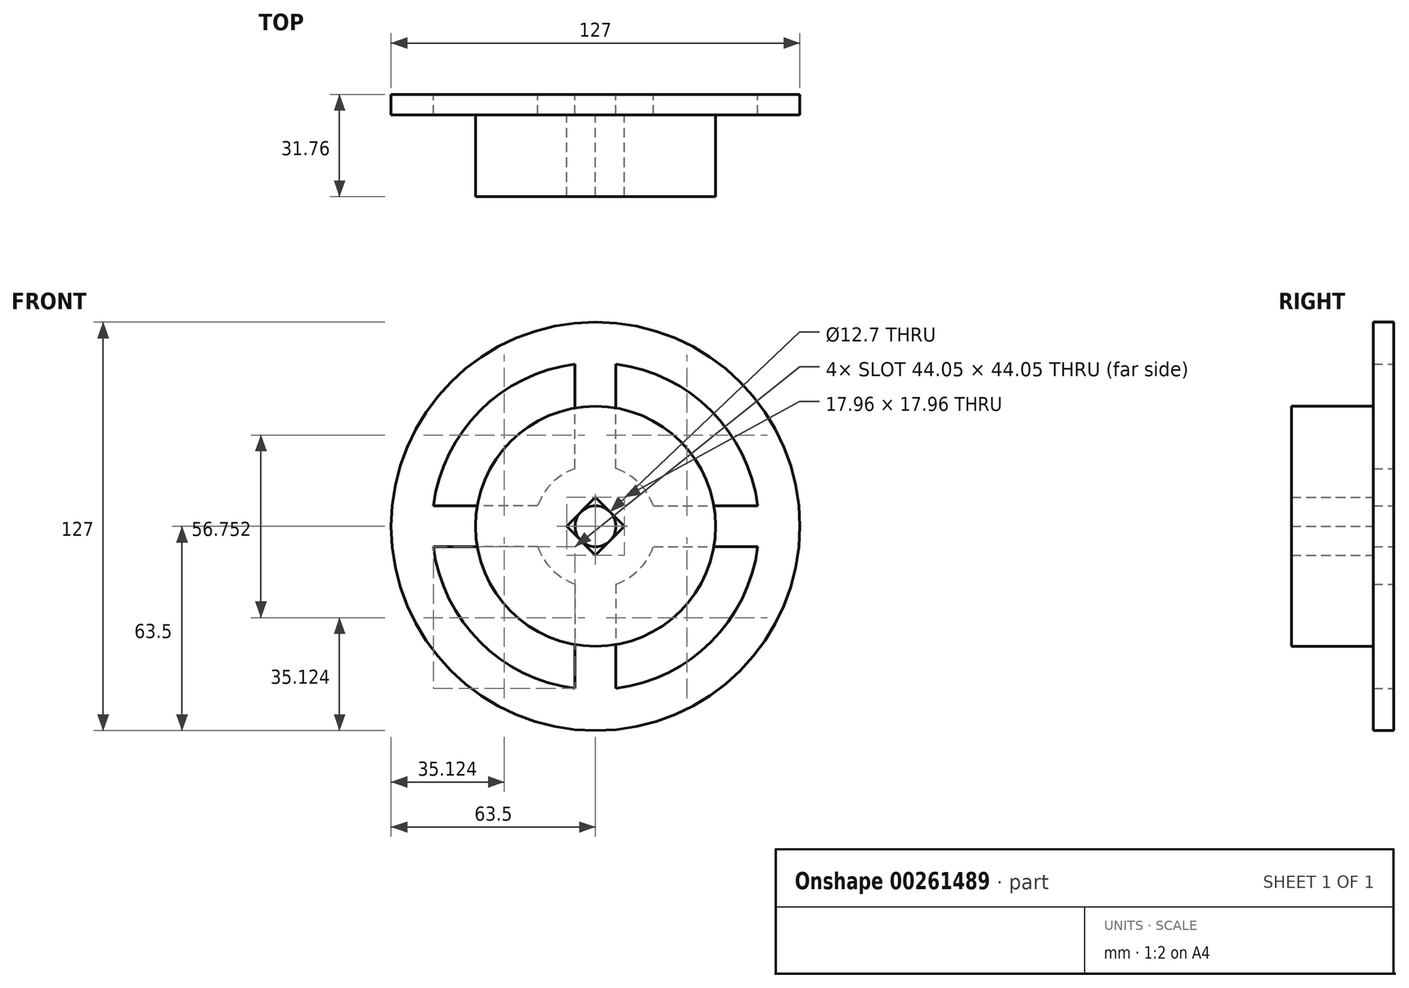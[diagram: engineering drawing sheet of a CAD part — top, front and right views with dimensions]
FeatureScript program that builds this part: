
annotation { "Feature Type Name" : "Feature", "Feature Type Description" : "" }
export const myFeature = defineFeature(function(context is Context, id is Id, definition is map)
    precondition{}
    {
        {
            var Q0;
            Q0=qCreatedBy(makeId("Front.planeOp"),FACE);
            var sketch = newSketch(context, id + "F0", { "sketchPlane" : qUnion([Q0])});
            skCircle(sketch, "E0", {"center": v(0, 0) * mm, "radius": 63.5 * mm});
            skArc(sketch, "E1", {"start": v(-50.4, -6.35) * mm, "mid": v(-35.92, -35.92) * mm, "end": v(-6.35, -50.4) * mm});
            skArc(sketch, "E2", {"start": v(17.96, 6.35) * mm, "mid": v(13.47, 13.47) * mm, "end": v(6.35, 17.96) * mm});
            skCircle(sketch, "E3", {"center": v(0, 0) * mm, "radius": 6.35 * mm});
            skLineSegment(sketch, "E4", {"start": v(0, 0) * mm, "end": v(0, 50.8) * mm, "construction": true});
            skLineSegment(sketch, "E5", {"start": v(0, 0) * mm, "end": v(50.8, 0) * mm, "construction": true});
            skLineSegment(sketch, "E6", {"start": v(0, 0) * mm, "end": v(0, -50.8) * mm, "construction": true});
            skLineSegment(sketch, "E7", {"start": v(0, 0) * mm, "end": v(-50.8, 0) * mm, "construction": true});
            skArc(sketch, "E8.trimOffspring", {"start": v(-6.35, 50.4) * mm, "mid": v(-35.92, 35.92) * mm, "end": v(-50.4, 6.35) * mm});
            skArc(sketch, "E9.trimOffspring", {"start": v(50.4, 6.35) * mm, "mid": v(35.92, 35.92) * mm, "end": v(6.35, 50.4) * mm});
            skArc(sketch, "E10.trimOffspring", {"start": v(6.35, -50.4) * mm, "mid": v(35.92, -35.92) * mm, "end": v(50.4, -6.35) * mm});
            skArc(sketch, "E11.trimOffspring", {"start": v(-6.35, 17.96) * mm, "mid": v(-13.47, 13.47) * mm, "end": v(-17.96, 6.35) * mm});
            skArc(sketch, "E12.trimOffspring", {"start": v(-17.96, -6.35) * mm, "mid": v(-13.47, -13.47) * mm, "end": v(-6.35, -17.96) * mm});
            skArc(sketch, "E13.trimOffspring", {"start": v(6.35, -17.96) * mm, "mid": v(13.47, -13.47) * mm, "end": v(17.96, -6.35) * mm});
            skLineSegment(sketch, "E14.trimOffspring", {"start": v(17.96, -6.35) * mm, "end": v(50.4, -6.35) * mm});
            skLineSegment(sketch, "E15.trimOffspring", {"start": v(6.35, -17.96) * mm, "end": v(6.35, -50.4) * mm});
            skLineSegment(sketch, "E16.trimOffspring", {"start": v(-6.35, -17.96) * mm, "end": v(-6.35, -50.4) * mm});
            skLineSegment(sketch, "E17.trimOffspring", {"start": v(-17.96, -6.35) * mm, "end": v(-50.4, -6.35) * mm});
            skLineSegment(sketch, "E18.trimOffspring", {"start": v(-17.96, 6.35) * mm, "end": v(-50.4, 6.35) * mm});
            skLineSegment(sketch, "E19.trimOffspring", {"start": v(-6.35, 17.96) * mm, "end": v(-6.35, 50.4) * mm});
            skLineSegment(sketch, "E20.trimOffspring", {"start": v(6.35, 17.96) * mm, "end": v(6.35, 50.4) * mm});
            skLineSegment(sketch, "E21.trimOffspring", {"start": v(17.96, 6.35) * mm, "end": v(50.4, 6.35) * mm});
            skLineSegment(sketch, "E22.0", {"start": v(-6.35, 17.96) * mm, "end": v(-6.35, 50.8) * mm});
            skSolve(sketch);
        }
        {
            var Q0;
            Q0=qSketchRegion(id+"F0",true);
            extrude(context, id + "F1", {"entities" : qUnion([Q0]), "endBound" : BoundingType.SYMMETRIC, "depth" : 6.35 * mm});
        }
        {
            var Q0;
            Q0=makeQuery(id+"F1.opExtrude","CAP_FACE",FACE,{"disambiguationData":[OSD([sQuery(id+"F0.wireOp",EDGE,"E0"),sQuery(id+"F0.wireOp",EDGE,"E1"),sQuery(id+"F0.wireOp",EDGE,"E2"),sQuery(id+"F0.wireOp",EDGE,"E3"),sQuery(id+"F0.wireOp",EDGE,"E8.trimOffspring"),sQuery(id+"F0.wireOp",EDGE,"E9.trimOffspring"),sQuery(id+"F0.wireOp",EDGE,"E10.trimOffspring"),sQuery(id+"F0.wireOp",EDGE,"E11.trimOffspring"),sQuery(id+"F0.wireOp",EDGE,"E12.trimOffspring"),sQuery(id+"F0.wireOp",EDGE,"E13.trimOffspring"),sQuery(id+"F0.wireOp",EDGE,"E14.trimOffspring"),sQuery(id+"F0.wireOp",EDGE,"E15.trimOffspring"),sQuery(id+"F0.wireOp",EDGE,"E16.trimOffspring"),sQuery(id+"F0.wireOp",EDGE,"E17.trimOffspring"),sQuery(id+"F0.wireOp",EDGE,"E18.trimOffspring"),sQuery(id+"F0.wireOp",EDGE,"E20.trimOffspring"),sQuery(id+"F0.wireOp",EDGE,"E21.trimOffspring"),sQuery(id+"F0.wireOp",EDGE,"E22.0")])],"isStart":false});
            var sketch = newSketch(context, id + "F2", { "sketchPlane" : qUnion([Q0])});
            skLineSegment(sketch, "E23.0", {"start": v(-40.13, 31.15) * mm, "end": v(31.15, -40.13) * mm});
            skLineSegment(sketch, "E24.0", {"start": v(-31.15, 40.13) * mm, "end": v(40.13, -31.15) * mm});
            skLineSegment(sketch, "E25.0", {"start": v(40.13, 31.15) * mm, "end": v(-31.15, -40.13) * mm});
            skLineSegment(sketch, "E26.0", {"start": v(31.15, 40.13) * mm, "end": v(-40.13, -31.15) * mm});
            skCircle(sketch, "E27", {"center": v(0, 0) * mm, "radius": 37.3 * mm});
            skSolve(sketch);
        }
        {
            var Q0;
            Q0 = qSketchRegion(id + "F2", true);
            extrude(context, id + "F3", {"entities" : qUnion([Q0]), "depth" : 25.4 * mm});
        }
    });
